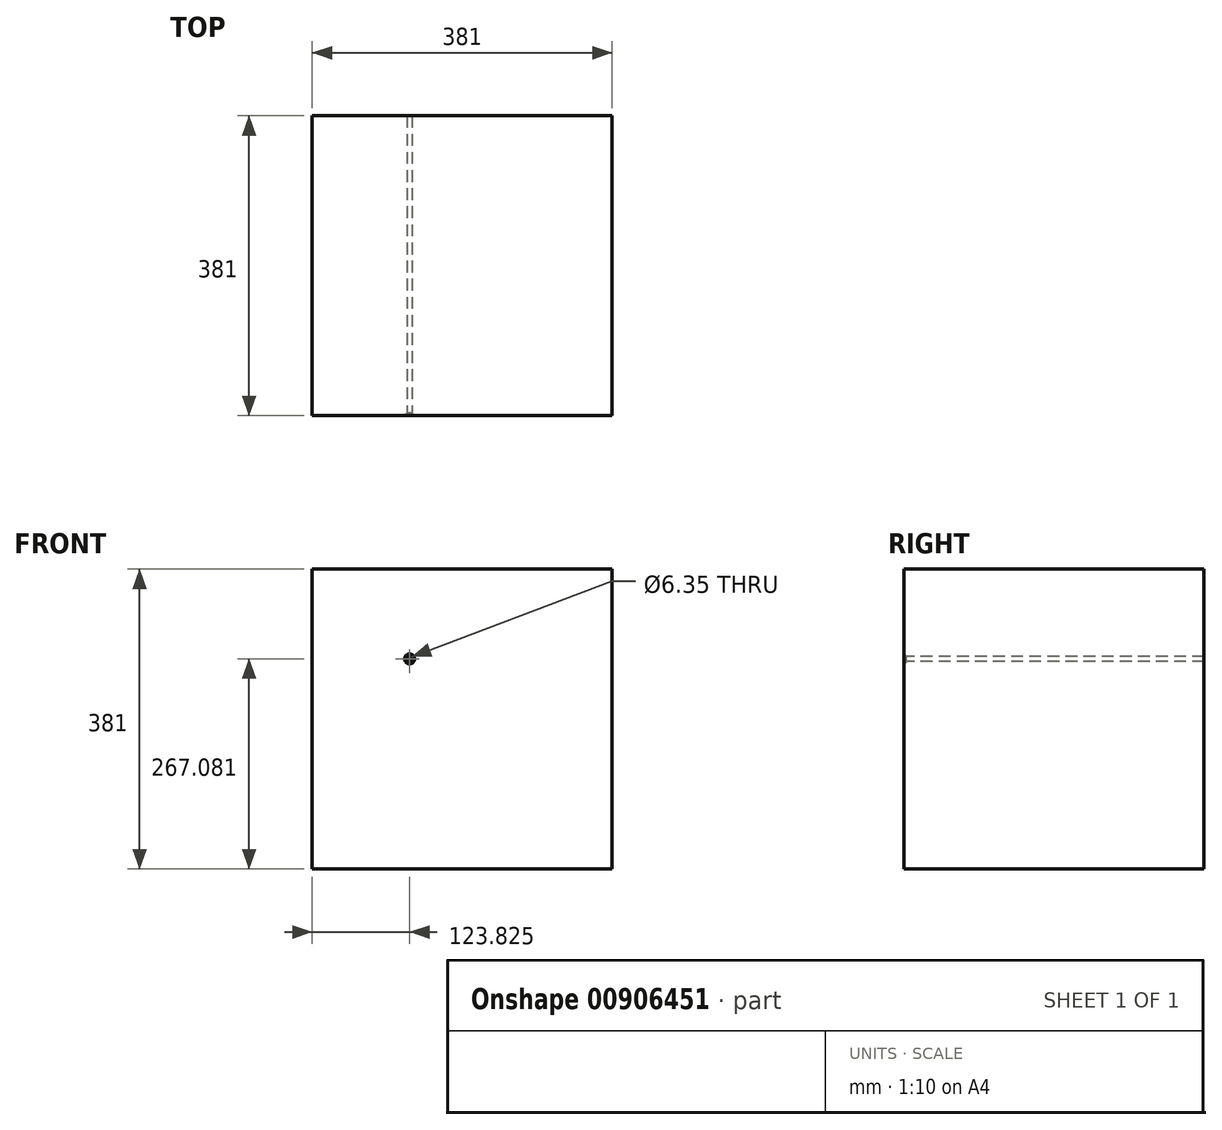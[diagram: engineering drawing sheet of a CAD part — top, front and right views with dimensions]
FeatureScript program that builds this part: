
annotation { "Feature Type Name" : "Feature", "Feature Type Description" : "" }
export const myFeature = defineFeature(function(context is Context, id is Id, definition is map)
    precondition{}
    {
        {
            var Q0;
            Q0=qCreatedBy(makeId("Front.planeOp"),FACE);
            var sketch = newSketch(context, id + "F0", { "sketchPlane" : qUnion([Q0])});
            skLineSegment(sketch, "E0.bottom", {"start": v(0, 0) * mm, "end": v(381, 0) * mm});
            skLineSegment(sketch, "E0.top", {"start": v(0, 381) * mm, "end": v(381, 381) * mm});
            skLineSegment(sketch, "E0.left", {"start": v(0, 0) * mm, "end": v(0, 381) * mm});
            skLineSegment(sketch, "E0.right", {"start": v(381, 0) * mm, "end": v(381, 381) * mm});
            skSolve(sketch);
        }
        {
            var Q0;
            Q0=qSketchRegion(id+"F0",true);
            extrude(context, id + "F1", {"entities" : qUnion([Q0]), "depth" : 381 * mm, "offsetDistance" : 25.4 * mm});
        }
        {
            var Q0;
            Q0=makeQuery(id+"F1.opExtrude","CAP_FACE",FACE,{"disambiguationData":[OSD([sQuery(id+"F0.wireOp",EDGE,"E0.bottom"),sQuery(id+"F0.wireOp",EDGE,"E0.top"),sQuery(id+"F0.wireOp",EDGE,"E0.left"),sQuery(id+"F0.wireOp",EDGE,"E0.right")])],"isStart":false});
            var sketch = newSketch(context, id + "F2", { "sketchPlane" : qUnion([Q0])});
            skPoint(sketch, "E1", {"position": v(123.83, 267.08) * mm});
            skSolve(sketch);
        }
        {
            var Q0;
            Q0=sQuery(id+"F2.wireOp",VERTEX,"E1");
            var Q1;
            Q1=makeQuery(id+"F1.opExtrude","SWEPT_BODY",BODY,{"disambiguationData":[OSD([sQuery(id+"F0.wireOp",EDGE,"E0.bottom"),sQuery(id+"F0.wireOp",EDGE,"E0.top"),sQuery(id+"F0.wireOp",EDGE,"E0.left"),sQuery(id+"F0.wireOp",EDGE,"E0.right")])]});
            hole(context, id + "F3", {"style" : HoleStyle.C_SINK, "endStyle" : HoleEndStyle.THROUGH, "holeDiameter" : 6.35 * mm, "cSinkDiameter" : 12.7 * mm, "cSinkAngle" : 90 * degree, "majorDiameter" : 6.35 * mm, "isTappedThrough" : true, "tappedDepth" : 12.7 * mm, "tapClearance" : 3, "locations" : qUnion([Q0]), "scope" : qUnion([Q1])});
        }
    });
